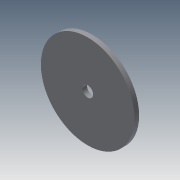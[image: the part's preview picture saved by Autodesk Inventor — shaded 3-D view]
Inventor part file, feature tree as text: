
AUTODESK INVENTOR PART (.ipt)
format: ipt  version: 2013 (Build 170138000, 138)  size: 75,776 bytes
history: native  units: mm
features: extrude x2, sketch x2
ambient origin geometry x8: Origin, YZ Plane, XZ Plane, XY Plane, X Axis, Y Axis, Z Axis, Center Point
bodies: Solid1 (feature_tree)
feature tree (4):
  extrude  "Extrusion1"  Depth=3.0mm TaperAngle=0.0deg
  extrude  "Extrusion2"  Depth=3.0mm TaperAngle=0.0deg
  sketch  "Sketch1"  dims[d0=60.191mm d1=3.0mm d2=0.0mm]
  sketch  "Sketch2"  dims[d3=7.0mm d5=3.0mm d6=0.0mm]
